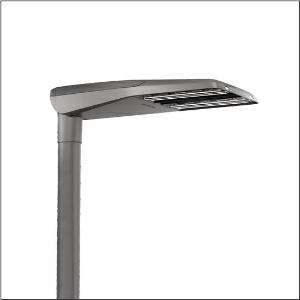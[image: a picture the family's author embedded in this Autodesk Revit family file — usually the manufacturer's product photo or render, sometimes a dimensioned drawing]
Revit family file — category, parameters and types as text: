
# Revit family: streetlight_sl_11_iq_midi___st1_2a_5xc3a41f08le_475e
name_source: partatom
category: Lighting Fixtures
units: mm (PartAtom-declared; Revit-internal decimal feet)

## family parameters
Cut with Voids When Loaded = No
Host = Face
Light Source = No
Part Type = Normal
Room Calculation Point = No
Round Connector Dimension = Use Diameter
Shared = No

## types (1)
- --- (1 x LED, 9590 lm, 60.4 W, 4000K)
    Apparent Load = 60 VA
    CIE Flux Codes = 32 70 96 100 100
    Color Rendering = 70
    Color Temperature = 4000K
    Default Elevation = 1800 mm
    Description = Streetlight SL 11 iQ midi, mast luminaire, primary light control with 3 zone facetted reflector, of plastic, silver coated, highly specular, primary optical cover: cover, of PMMA, transparent, light distribution: ST1.2a, light emission: direct distribution, primary light characteristic: asymmetric, installation type: post-top, side-entry, LED, High Power LED, rated luminous flux: 9.590lm, luminous efficacy: 159lm/W, light colour: 740, colour temperature: 4000K, control: Street-Remote, optimised constant luminous flux control (CLO 2.0), Desk-Remote (wireless, voltage-free reading and setting of iQ features in the workshop via application-optimized NFC function/RFID function), Light-Fading, Smart-Wire, Night-Set, Lumen-Switch, Temp-Guard, Auto-Match, with cable H07RN-F 5x 1.5mm², mains connection: 230..240V, AC, 50/60Hz, connection cable pre-assembled, cable length: 8,5m, start of lifetime: 60W, end of service life: 63W, reduction: 30W, luminaire housing, of diecast aluminium, powder-coated, Siteco® metallic grey (DB 702S), please order mast flange separately, inclination adjustable without tools: 0°, 5°, 10°, 15° (post-top) | 0°, -5°, -10°, -15° (side-entry), sealing non-destructively replaceable, multi-level sealing system, length: 780mm, width: 376mm, height: 118mm, mast flange for spigot size: 42mm (side-entry): 5XC10008XM4, 60/48mm (side-entry/post-top): 5XC10108XM2, 76/60mm (side-entry/post-top): 5XC10108XM1, equipment: standard, protection rating (complete): IP66, insulation class (complete): insulation class II (safety insulation), certification: CE, ENEC, VDE, impact resistance: IK09, permissible operating ambient temperature for outdoor applications: -25..+50°C, standard-compliant lighting for roads and squares, Environmental Product Declaration (EPD) tested and certified by an independent institute, packaging unit: 1 piece

Light Distribution: ST1.2a
    Height = 118 mm
    Lamp = 1 x LED
    Lamp Light Flux = 9590 lm
    Lamp Power = 60.4 W
    Lamp count = 1
    Length = 780 mm
    Luminous efficacy = 159 lm/W
    Manufacturer = Siteco
    ModVariant = No
    Model = 5XC3A41F08LE
    Number of Poles = 1
    OnlyDefault = Yes
    Power Factor = 1
    Product Name = Streetlight SL 11 iQ midi | ST1.2a
    Product group = mast luminaire | pylon top
    ProductGroupID = 6100
    Protection Class = Protection class II
    Protection Degree = IP 66
    RLX_Detail_Level = 1
    RLX_Emergency_Light_Flux = 0 lm
    RLX_Emergency_Type = 0
    RLX_Emergency_Type_DB = No
    RlxData = <blob elided: 70605 chars, md5=3523328b>
    Socket = socket
    Standby Power = 0 W
    System Light Flux = 9590 lm
    System Power = 60 W
    Type Comments = factory setting: luminous flux: 100 % | dim-lin: 254 | 520 mA
    Type Image = l_1005960.jpg
    URL = http://relux.com
    VarID = @adj_132789
    Voltage = 0 V
    Weight = 0.00 kg
    Width = 376 mm

## geometry (parser evidence)
native form markers: Blend x4, Sweep x10
no freeform markers — native parametric forms only
